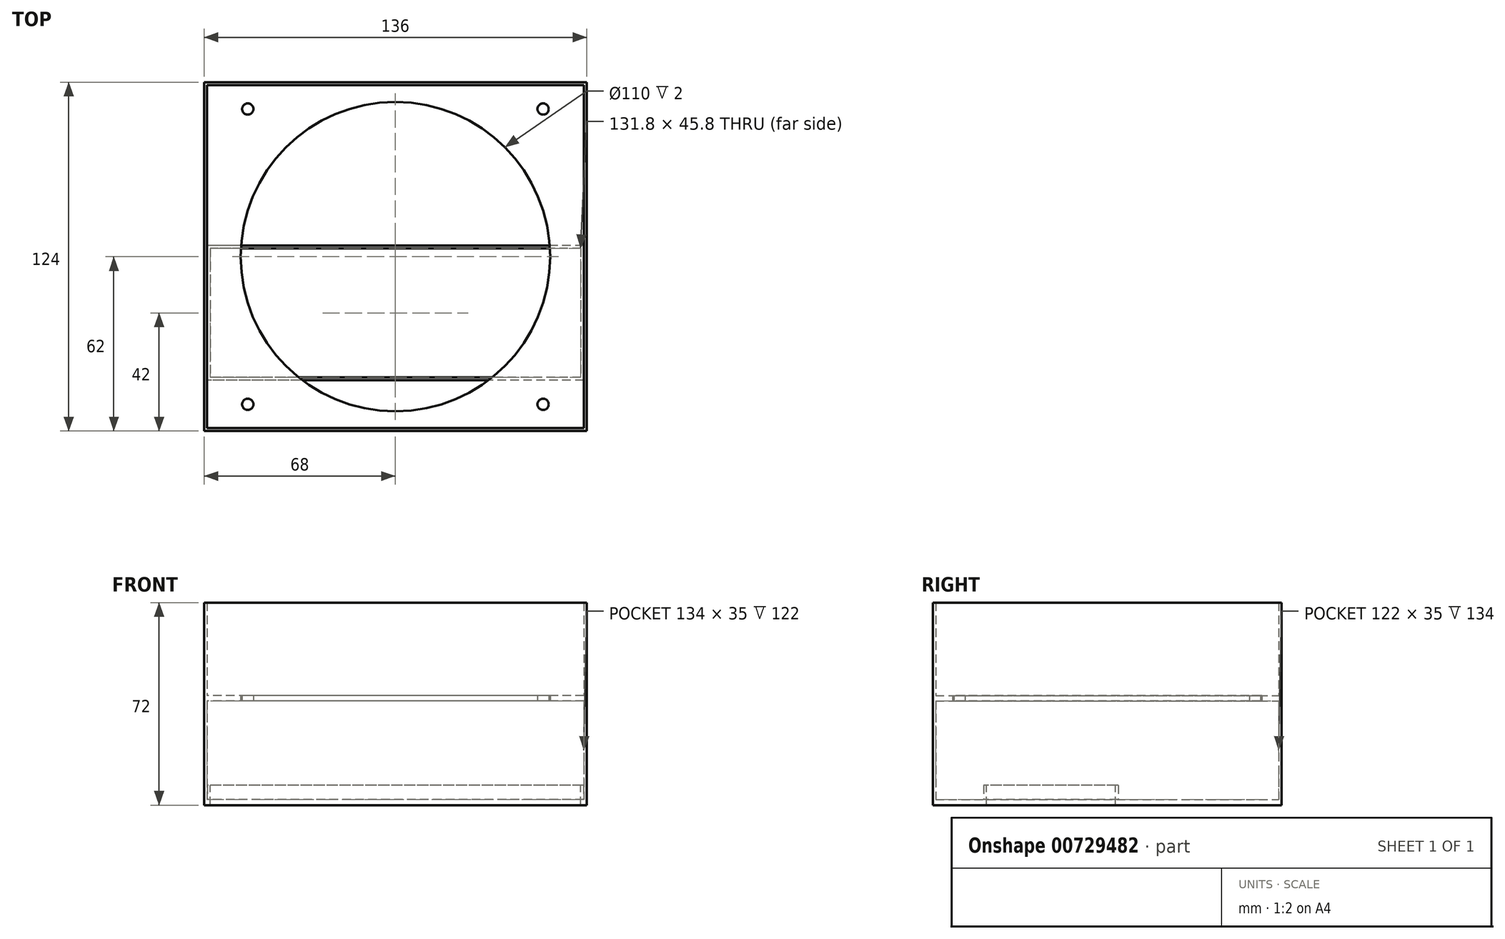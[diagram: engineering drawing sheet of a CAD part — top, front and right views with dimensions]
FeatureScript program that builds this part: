
annotation { "Feature Type Name" : "Feature", "Feature Type Description" : "" }
export const myFeature = defineFeature(function(context is Context, id is Id, definition is map)
    precondition{}
    {
        {
            var Q0;
            Q0=qCreatedBy(makeId("Top.planeOp"),FACE);
            var sketch = newSketch(context, id + "F0", { "sketchPlane" : qUnion([Q0])});
            skLineSegment(sketch, "E0.bottom", {"start": v(67, -61) * mm, "end": v(-67, -61) * mm});
            skLineSegment(sketch, "E0.top", {"start": v(67, 61) * mm, "end": v(-67, 61) * mm});
            skLineSegment(sketch, "E0.left", {"start": v(67, -61) * mm, "end": v(67, 61) * mm});
            skLineSegment(sketch, "E0.right", {"start": v(-67, -61) * mm, "end": v(-67, 61) * mm});
            skPoint(sketch, "E0.middle", {"position": v(0, 0) * mm});
            skCircle(sketch, "E1", {"center": v(0, 0) * mm, "radius": 55 * mm});
            skPoint(sketch, "E2", {"position": v(-52.5, 52.5) * mm});
            skPoint(sketch, "E3", {"position": v(-52.5, -52.5) * mm});
            skPoint(sketch, "E4", {"position": v(52.5, -52.5) * mm});
            skPoint(sketch, "E5", {"position": v(52.5, 52.5) * mm});
            skCircle(sketch, "E6", {"center": v(-52.5, 52.5) * mm, "radius": 2 * mm});
            skCircle(sketch, "E7", {"center": v(52.5, 52.5) * mm, "radius": 2 * mm});
            skCircle(sketch, "E8", {"center": v(52.5, -52.5) * mm, "radius": 2 * mm});
            skCircle(sketch, "E9", {"center": v(-52.5, -52.5) * mm, "radius": 2 * mm});
            skLineSegment(sketch, "E10.0", {"start": v(68, 62) * mm, "end": v(-68, 62) * mm});
            skLineSegment(sketch, "E10.1", {"start": v(68, -62) * mm, "end": v(68, 62) * mm});
            skLineSegment(sketch, "E10.2", {"start": v(68, -62) * mm, "end": v(-68, -62) * mm});
            skLineSegment(sketch, "E10.3", {"start": v(-68, -62) * mm, "end": v(-68, 62) * mm});
            skSolve(sketch);
        }
        {
            var Q0;
            Q0=makeQuery(id+"F0.imprint","IMPRINT",FACE,{"disambiguationData":[TD([[makeQuery(id+"F0.imprint","IMPRINT",EDGE,{"derivedFrom":sQuery(id+"F0.wireOp",EDGE,"E0.bottom")}),-1.0]])]});
            extrude(context, id + "F1", {"entities" : qUnion([Q0]), "depth" : 2 * mm, "offsetDistance" : 25 * mm});
        }
        {
            var Q0;
            Q0=makeQuery(id+"F0.imprint","IMPRINT",FACE,{"disambiguationData":[TD([[makeQuery(id+"F0.imprint","IMPRINT",EDGE,{"derivedFrom":sQuery(id+"F0.wireOp",EDGE,"E0.bottom")}),1.0]])]});
            extrude(context, id + "F2", {"entities" : qUnion([Q0]), "operationType" : NewBodyOperationType.ADD, "endBound" : BoundingType.SYMMETRIC, "depth" : 70 * mm, "offsetDistance" : 25 * mm});
        }
        {
            var Q0;
            Q0=makeQuery(id+"F2.opExtrude","CAP_FACE",FACE,{"disambiguationData":[OSD([sQuery(id+"F0.wireOp",EDGE,"E0.bottom"),sQuery(id+"F0.wireOp",EDGE,"E0.top"),sQuery(id+"F0.wireOp",EDGE,"E0.left"),sQuery(id+"F0.wireOp",EDGE,"E0.right"),sQuery(id+"F0.wireOp",EDGE,"E10.0"),sQuery(id+"F0.wireOp",EDGE,"E10.1"),sQuery(id+"F0.wireOp",EDGE,"E10.2"),sQuery(id+"F0.wireOp",EDGE,"E10.3")])],"isStart":true});
            var sketch = newSketch(context, id + "F3", { "sketchPlane" : qUnion([Q0])});
            skLineSegment(sketch, "E11.bottom", {"start": v(-68, 62) * mm, "end": v(68, 62) * mm});
            skLineSegment(sketch, "E11.top", {"start": v(-68, -62) * mm, "end": v(68, -62) * mm});
            skLineSegment(sketch, "E11.left", {"start": v(-68, 62) * mm, "end": v(-68, -62) * mm});
            skLineSegment(sketch, "E11.right", {"start": v(68, 62) * mm, "end": v(68, -62) * mm});
            skPoint(sketch, "E11.middle", {"position": v(0, 0) * mm});
            skPoint(sketch, "E12", {"position": v(0, 20) * mm});
            skLineSegment(sketch, "E13.bottom", {"start": v(65.9, -2.9) * mm, "end": v(-65.9, -2.9) * mm});
            skLineSegment(sketch, "E13.top", {"start": v(65.9, 42.9) * mm, "end": v(-65.9, 42.9) * mm});
            skLineSegment(sketch, "E13.left", {"start": v(65.9, -2.9) * mm, "end": v(65.9, 42.9) * mm});
            skLineSegment(sketch, "E13.right", {"start": v(-65.9, -2.9) * mm, "end": v(-65.9, 42.9) * mm});
            skLineSegment(sketch, "E14.0", {"start": v(66.9, 43.9) * mm, "end": v(-66.9, 43.9) * mm});
            skLineSegment(sketch, "E14.1", {"start": v(66.9, -3.9) * mm, "end": v(66.9, 43.9) * mm});
            skLineSegment(sketch, "E14.2", {"start": v(66.9, -3.9) * mm, "end": v(-66.9, -3.9) * mm});
            skLineSegment(sketch, "E14.3", {"start": v(-66.9, -3.9) * mm, "end": v(-66.9, 43.9) * mm});
            skSolve(sketch);
        }
        {
            var Q0;
            Q0=makeQuery(id+"F3.imprint","IMPRINT",FACE,{"disambiguationData":[TD([[makeQuery(id+"F3.imprint","IMPRINT",EDGE,{"derivedFrom":sQuery(id+"F3.wireOp",EDGE,"E14.0")}),-1.0]])]});
            var Q1;
            Q1=makeQuery(id+"F3.imprint","IMPRINT",FACE,{"disambiguationData":[TD([[makeQuery(id+"F3.imprint","IMPRINT",EDGE,{"derivedFrom":sQuery(id+"F3.wireOp",EDGE,"E11.bottom")}),1.0]])]});
            var Q2;
            Q2=makeQuery(id+"F3.imprint","IMPRINT",FACE,{"disambiguationData":[TD([[makeQuery(id+"F3.imprint","IMPRINT",EDGE,{"derivedFrom":sQuery(id+"F3.wireOp",EDGE,"E13.bottom")}),1.0]])]});
            extrude(context, id + "F4", {"entities" : qUnion([Q0, Q1, Q2]), "operationType" : NewBodyOperationType.ADD, "depth" : 2 * mm, "offsetDistance" : 25 * mm});
        }
        {
            var Q0;
            Q0=makeQuery(id+"F3.imprint","IMPRINT",FACE,{"disambiguationData":[TD([[makeQuery(id+"F3.imprint","IMPRINT",EDGE,{"derivedFrom":sQuery(id+"F3.wireOp",EDGE,"E13.bottom")}),1.0]])]});
            extrude(context, id + "F5", {"entities" : qUnion([Q0]), "operationType" : NewBodyOperationType.ADD, "oppositeDirection" : true, "depth" : 5 * mm, "offsetDistance" : 25 * mm});
        }
    });
